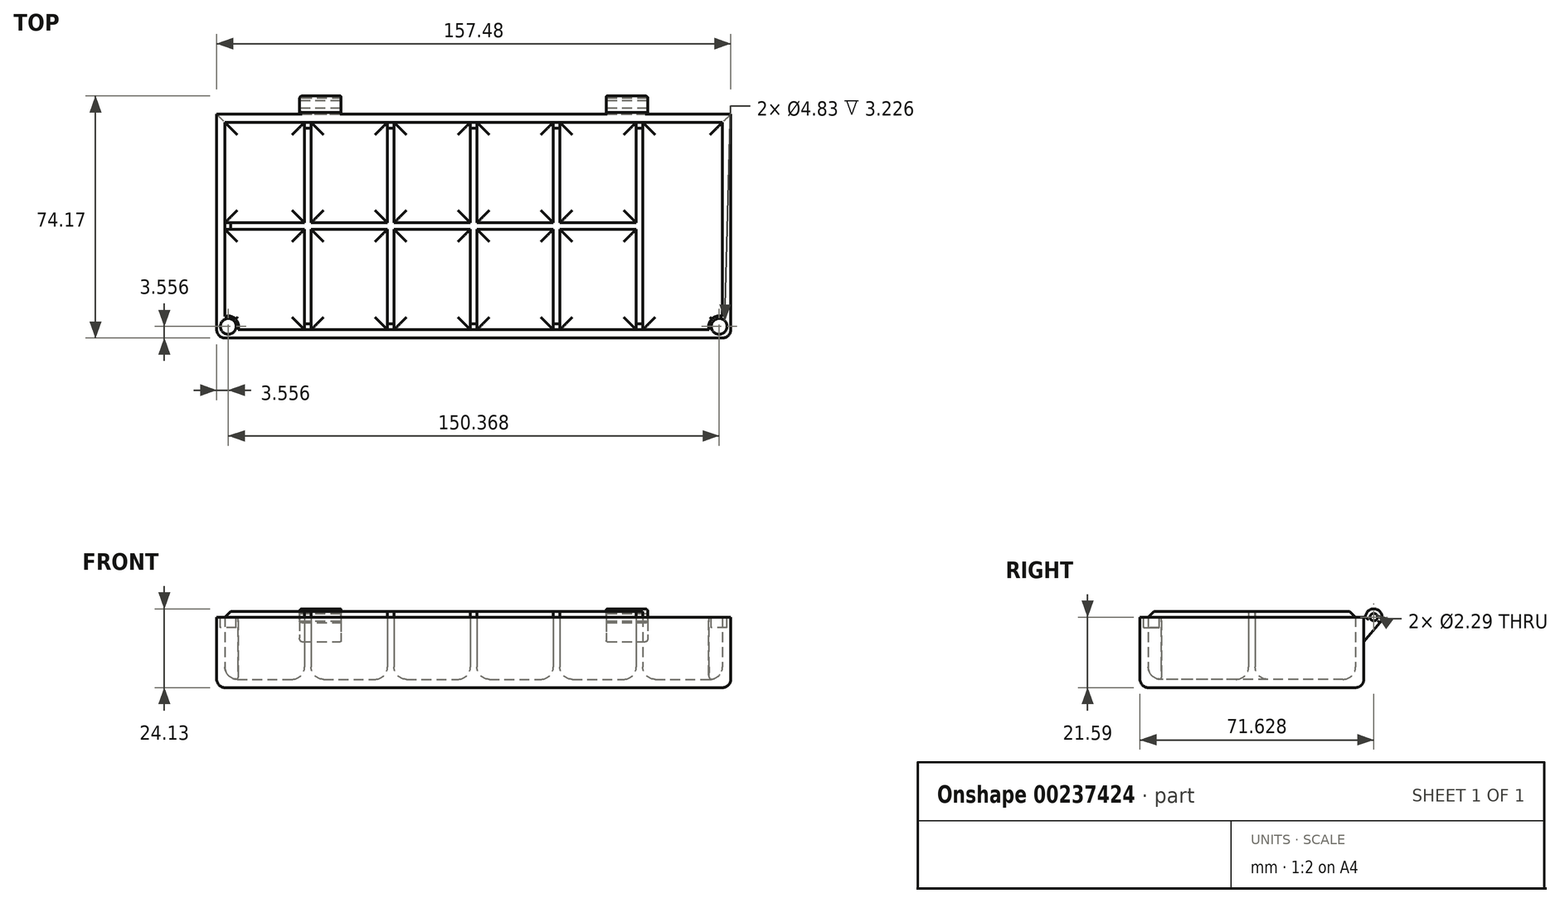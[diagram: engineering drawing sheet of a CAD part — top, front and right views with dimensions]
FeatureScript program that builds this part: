
annotation { "Feature Type Name" : "Feature", "Feature Type Description" : "" }
export const myFeature = defineFeature(function(context is Context, id is Id, definition is map)
    precondition{}
    {
        {
            var Q0;
            Q0=qCreatedBy(makeId("Top.planeOp"),FACE);
            var sketch = newSketch(context, id + "F0", { "sketchPlane" : qUnion([Q0])});
            skLineSegment(sketch, "E0.bottom", {"start": v(-78.74, 34.29) * mm, "end": v(78.74, 34.3) * mm});
            skLineSegment(sketch, "E0.top", {"start": v(-78.74, -34.3) * mm, "end": v(78.74, -34.3) * mm});
            skLineSegment(sketch, "E0.left", {"start": v(-78.74, 34.29) * mm, "end": v(-78.74, -34.3) * mm});
            skLineSegment(sketch, "E0.right", {"start": v(78.74, 34.3) * mm, "end": v(78.74, -34.3) * mm});
            skSolve(sketch);
        }
        {
            var Q0;
            Q0 = qSketchRegion(id + "F0", true);
            extrude(context, id + "F1", {"entities" : qUnion([Q0]), "depth" : 2.54 * mm});
        }
        {
            var Q0;
            Q0=makeQuery(id+"F1.opExtrude","CAP_FACE",FACE,{"disambiguationData":[OSD([sQuery(id+"F0.wireOp",EDGE,"E0.bottom"),sQuery(id+"F0.wireOp",EDGE,"E0.top"),sQuery(id+"F0.wireOp",EDGE,"E0.left"),sQuery(id+"F0.wireOp",EDGE,"E0.right")])],"isStart":false});
            var sketch = newSketch(context, id + "F2", { "sketchPlane" : qUnion([Q0])});
            skLineSegment(sketch, "E1.bottom", {"start": v(-78.74, 34.29) * mm, "end": v(78.74, 34.29) * mm});
            skLineSegment(sketch, "E1.top", {"start": v(-78.74, -34.3) * mm, "end": v(78.74, -34.3) * mm});
            skLineSegment(sketch, "E1.left", {"start": v(-78.74, 34.29) * mm, "end": v(-78.74, -34.3) * mm});
            skLineSegment(sketch, "E1.right", {"start": v(78.74, 34.29) * mm, "end": v(78.74, -34.3) * mm});
            skLineSegment(sketch, "E2.bottom", {"start": v(-76.2, 31.75) * mm, "end": v(-51.82, 31.75) * mm});
            skLineSegment(sketch, "E2.top", {"start": v(-76.2, -31.75) * mm, "end": v(-51.82, -31.75) * mm});
            skLineSegment(sketch, "E2.left", {"start": v(-76.2, 31.75) * mm, "end": v(-76.2, 1.02) * mm});
            skLineSegment(sketch, "E2.right", {"start": v(76.2, 31.75) * mm, "end": v(76.2, -31.75) * mm});
            skLineSegment(sketch, "E3", {"start": v(-76.2, 1.02) * mm, "end": v(-51.82, 1.02) * mm});
            skLineSegment(sketch, "E4", {"start": v(-76.2, -1.02) * mm, "end": v(-51.82, -1.02) * mm});
            skLineSegment(sketch, "E5", {"start": v(-51.82, 31.75) * mm, "end": v(-51.82, 1.02) * mm});
            skLineSegment(sketch, "E6", {"start": v(-49.78, 31.75) * mm, "end": v(-49.78, 1.02) * mm});
            skLineSegment(sketch, "E7.trimOffspring", {"start": v(-51.82, -1.02) * mm, "end": v(-51.82, -31.75) * mm});
            skLineSegment(sketch, "E8.trimOffspring", {"start": v(-49.78, -1.02) * mm, "end": v(-49.78, -31.75) * mm});
            skLineSegment(sketch, "E9.trimOffspring", {"start": v(-49.78, 1.02) * mm, "end": v(-26.42, 1.02) * mm});
            skLineSegment(sketch, "E10.trimOffspring", {"start": v(-49.78, -1.02) * mm, "end": v(-26.42, -1.02) * mm});
            skLineSegment(sketch, "E11.trimOffspring", {"start": v(-76.2, -1.02) * mm, "end": v(-76.2, -31.75) * mm});
            skLineSegment(sketch, "E12.trimOffspring", {"start": v(-49.78, -31.75) * mm, "end": v(-26.42, -31.75) * mm});
            skLineSegment(sketch, "E13.trimOffspring", {"start": v(-49.78, 31.75) * mm, "end": v(-26.42, 31.75) * mm});
            skLineSegment(sketch, "E14.1.0.0", {"start": v(-24.38, 31.75) * mm, "end": v(-24.38, 1.02) * mm});
            skLineSegment(sketch, "E14.1.0.1", {"start": v(-26.42, 31.75) * mm, "end": v(-26.42, 1.02) * mm});
            skLineSegment(sketch, "E14.1.0.2", {"start": v(-24.38, -1.02) * mm, "end": v(-24.38, -31.75) * mm});
            skLineSegment(sketch, "E14.1.0.3", {"start": v(-26.42, -1.02) * mm, "end": v(-26.42, -31.75) * mm});
            skLineSegment(sketch, "E14.2.0.0", {"start": v(1.02, 31.75) * mm, "end": v(1.02, 1.02) * mm});
            skLineSegment(sketch, "E14.2.0.1", {"start": v(-1.02, 31.75) * mm, "end": v(-1.02, 1.02) * mm});
            skLineSegment(sketch, "E14.2.0.2", {"start": v(1.02, -1.02) * mm, "end": v(1.02, -31.75) * mm});
            skLineSegment(sketch, "E14.2.0.3", {"start": v(-1.02, -1.02) * mm, "end": v(-1.02, -31.75) * mm});
            skLineSegment(sketch, "E14.3.0.0", {"start": v(26.42, 31.75) * mm, "end": v(26.42, 1.02) * mm});
            skLineSegment(sketch, "E14.3.0.1", {"start": v(24.38, 31.75) * mm, "end": v(24.38, 1.02) * mm});
            skLineSegment(sketch, "E14.3.0.2", {"start": v(26.42, -1.02) * mm, "end": v(26.42, -31.75) * mm});
            skLineSegment(sketch, "E14.3.0.3", {"start": v(24.38, -1.02) * mm, "end": v(24.38, -31.75) * mm});
            skLineSegment(sketch, "E14.4.0.0", {"start": v(51.82, 31.75) * mm, "end": v(51.82, 1.02) * mm});
            skLineSegment(sketch, "E14.4.0.1", {"start": v(49.78, 31.75) * mm, "end": v(49.78, 1.02) * mm});
            skLineSegment(sketch, "E14.4.0.2", {"start": v(51.82, -1.02) * mm, "end": v(51.82, -31.75) * mm});
            skLineSegment(sketch, "E14.4.0.3", {"start": v(49.78, -1.02) * mm, "end": v(49.78, -31.75) * mm});
            skLineSegment(sketch, "E14.direction1", {"start": v(-51.82, -31.75) * mm, "end": v(-26.42, -31.75) * mm, "construction": true});
            skLineSegment(sketch, "E15.trimOffspring", {"start": v(-24.38, -31.75) * mm, "end": v(-1.02, -31.75) * mm});
            skLineSegment(sketch, "E16.trimOffspring", {"start": v(1.02, -31.75) * mm, "end": v(24.38, -31.75) * mm});
            skLineSegment(sketch, "E17.trimOffspring", {"start": v(26.42, -31.75) * mm, "end": v(49.78, -31.75) * mm});
            skLineSegment(sketch, "E18.trimOffspring", {"start": v(51.82, -31.75) * mm, "end": v(76.2, -31.75) * mm});
            skLineSegment(sketch, "E19.trimOffspring", {"start": v(26.42, 1.02) * mm, "end": v(49.78, 1.02) * mm});
            skLineSegment(sketch, "E20.trimOffspring", {"start": v(26.42, -1.02) * mm, "end": v(49.78, -1.02) * mm});
            skLineSegment(sketch, "E21.trimOffspring", {"start": v(1.02, 1.02) * mm, "end": v(24.38, 1.02) * mm});
            skLineSegment(sketch, "E22.trimOffspring", {"start": v(1.02, -1.02) * mm, "end": v(24.38, -1.02) * mm});
            skLineSegment(sketch, "E23.trimOffspring", {"start": v(-24.38, 1.02) * mm, "end": v(-1.02, 1.02) * mm});
            skLineSegment(sketch, "E24.trimOffspring", {"start": v(-24.38, -1.02) * mm, "end": v(-1.02, -1.02) * mm});
            skLineSegment(sketch, "E25.trimOffspring", {"start": v(-24.38, 31.75) * mm, "end": v(-1.02, 31.75) * mm});
            skLineSegment(sketch, "E26.trimOffspring", {"start": v(1.02, 31.75) * mm, "end": v(24.38, 31.75) * mm});
            skLineSegment(sketch, "E27.trimOffspring", {"start": v(26.42, 31.75) * mm, "end": v(49.78, 31.75) * mm});
            skLineSegment(sketch, "E28.trimOffspring", {"start": v(51.82, 31.75) * mm, "end": v(76.2, 31.75) * mm});
            skLineSegment(sketch, "E29", {"start": v(51.82, 1.02) * mm, "end": v(51.82, -1.02) * mm});
            skSolve(sketch);
        }
        {
            var Q0;
            Q0 = qSketchRegion(id + "F2", true);
            extrude(context, id + "F3", {"entities" : qUnion([Q0]), "operationType" : NewBodyOperationType.ADD, "depth" : 19.05 * mm});
        }
        {
            var Q0;
            Q0=makeQuery(id+"F3.boolean.opBoolean","SPLIT",FACE,{"disambiguationData":[TD([makeQuery(id+"F3.opExtrude","SWEPT_FACE",FACE,{"disambiguationData":[OSD([sQuery(id+"F2.wireOp",EDGE,"E2.bottom")])]})])],"derivedFrom":makeQuery(id+"F1.opExtrude","CAP_FACE",FACE,{"disambiguationData":[OSD([sQuery(id+"F0.wireOp",EDGE,"E0.bottom"),sQuery(id+"F0.wireOp",EDGE,"E0.top"),sQuery(id+"F0.wireOp",EDGE,"E0.left"),sQuery(id+"F0.wireOp",EDGE,"E0.right")])],"isStart":false})});
            var Q1;
            Q1=makeQuery(id+"F3.boolean.opBoolean","SPLIT",FACE,{"disambiguationData":[TD([makeQuery(id+"F3.opExtrude","SWEPT_FACE",FACE,{"disambiguationData":[OSD([sQuery(id+"F2.wireOp",EDGE,"E2.top")])]})])],"derivedFrom":makeQuery(id+"F1.opExtrude","CAP_FACE",FACE,{"disambiguationData":[OSD([sQuery(id+"F0.wireOp",EDGE,"E0.bottom"),sQuery(id+"F0.wireOp",EDGE,"E0.top"),sQuery(id+"F0.wireOp",EDGE,"E0.left"),sQuery(id+"F0.wireOp",EDGE,"E0.right")])],"isStart":false})});
            var Q2;
            Q2=makeQuery(id+"F3.boolean.opBoolean","SPLIT",FACE,{"disambiguationData":[TD([makeQuery(id+"F3.opExtrude","SWEPT_FACE",FACE,{"disambiguationData":[OSD([sQuery(id+"F2.wireOp",EDGE,"E8.trimOffspring")])]})])],"derivedFrom":makeQuery(id+"F1.opExtrude","CAP_FACE",FACE,{"disambiguationData":[OSD([sQuery(id+"F0.wireOp",EDGE,"E0.bottom"),sQuery(id+"F0.wireOp",EDGE,"E0.top"),sQuery(id+"F0.wireOp",EDGE,"E0.left"),sQuery(id+"F0.wireOp",EDGE,"E0.right")])],"isStart":false})});
            var Q3;
            Q3=makeQuery(id+"F3.boolean.opBoolean","SPLIT",FACE,{"disambiguationData":[TD([makeQuery(id+"F3.opExtrude","SWEPT_FACE",FACE,{"disambiguationData":[OSD([sQuery(id+"F2.wireOp",EDGE,"E6")])]})])],"derivedFrom":makeQuery(id+"F1.opExtrude","CAP_FACE",FACE,{"disambiguationData":[OSD([sQuery(id+"F0.wireOp",EDGE,"E0.bottom"),sQuery(id+"F0.wireOp",EDGE,"E0.top"),sQuery(id+"F0.wireOp",EDGE,"E0.left"),sQuery(id+"F0.wireOp",EDGE,"E0.right")])],"isStart":false})});
            var Q4;
            Q4=makeQuery(id+"F3.boolean.opBoolean","SPLIT",FACE,{"disambiguationData":[TD([makeQuery(id+"F3.opExtrude","SWEPT_FACE",FACE,{"disambiguationData":[OSD([sQuery(id+"F2.wireOp",EDGE,"E14.1.0.0")])]})])],"derivedFrom":makeQuery(id+"F1.opExtrude","CAP_FACE",FACE,{"disambiguationData":[OSD([sQuery(id+"F0.wireOp",EDGE,"E0.bottom"),sQuery(id+"F0.wireOp",EDGE,"E0.top"),sQuery(id+"F0.wireOp",EDGE,"E0.left"),sQuery(id+"F0.wireOp",EDGE,"E0.right")])],"isStart":false})});
            var Q5;
            Q5=makeQuery(id+"F3.boolean.opBoolean","SPLIT",FACE,{"disambiguationData":[TD([makeQuery(id+"F3.opExtrude","SWEPT_FACE",FACE,{"disambiguationData":[OSD([sQuery(id+"F2.wireOp",EDGE,"E14.1.0.2")])]})])],"derivedFrom":makeQuery(id+"F1.opExtrude","CAP_FACE",FACE,{"disambiguationData":[OSD([sQuery(id+"F0.wireOp",EDGE,"E0.bottom"),sQuery(id+"F0.wireOp",EDGE,"E0.top"),sQuery(id+"F0.wireOp",EDGE,"E0.left"),sQuery(id+"F0.wireOp",EDGE,"E0.right")])],"isStart":false})});
            var Q6;
            Q6=makeQuery(id+"F3.boolean.opBoolean","SPLIT",FACE,{"disambiguationData":[TD([makeQuery(id+"F3.opExtrude","SWEPT_FACE",FACE,{"disambiguationData":[OSD([sQuery(id+"F2.wireOp",EDGE,"E14.2.0.2")])]})])],"derivedFrom":makeQuery(id+"F1.opExtrude","CAP_FACE",FACE,{"disambiguationData":[OSD([sQuery(id+"F0.wireOp",EDGE,"E0.bottom"),sQuery(id+"F0.wireOp",EDGE,"E0.top"),sQuery(id+"F0.wireOp",EDGE,"E0.left"),sQuery(id+"F0.wireOp",EDGE,"E0.right")])],"isStart":false})});
            var Q7;
            Q7=makeQuery(id+"F3.boolean.opBoolean","SPLIT",FACE,{"disambiguationData":[TD([makeQuery(id+"F3.opExtrude","SWEPT_FACE",FACE,{"disambiguationData":[OSD([sQuery(id+"F2.wireOp",EDGE,"E14.2.0.0")])]})])],"derivedFrom":makeQuery(id+"F1.opExtrude","CAP_FACE",FACE,{"disambiguationData":[OSD([sQuery(id+"F0.wireOp",EDGE,"E0.bottom"),sQuery(id+"F0.wireOp",EDGE,"E0.top"),sQuery(id+"F0.wireOp",EDGE,"E0.left"),sQuery(id+"F0.wireOp",EDGE,"E0.right")])],"isStart":false})});
            var Q8;
            Q8=makeQuery(id+"F3.boolean.opBoolean","SPLIT",FACE,{"disambiguationData":[TD([makeQuery(id+"F3.opExtrude","SWEPT_FACE",FACE,{"disambiguationData":[OSD([sQuery(id+"F2.wireOp",EDGE,"E14.3.0.0")])]})])],"derivedFrom":makeQuery(id+"F1.opExtrude","CAP_FACE",FACE,{"disambiguationData":[OSD([sQuery(id+"F0.wireOp",EDGE,"E0.bottom"),sQuery(id+"F0.wireOp",EDGE,"E0.top"),sQuery(id+"F0.wireOp",EDGE,"E0.left"),sQuery(id+"F0.wireOp",EDGE,"E0.right")])],"isStart":false})});
            var Q9;
            Q9=makeQuery(id+"F3.boolean.opBoolean","SPLIT",FACE,{"disambiguationData":[TD([makeQuery(id+"F3.opExtrude","SWEPT_FACE",FACE,{"disambiguationData":[OSD([sQuery(id+"F2.wireOp",EDGE,"E14.3.0.2")])]})])],"derivedFrom":makeQuery(id+"F1.opExtrude","CAP_FACE",FACE,{"disambiguationData":[OSD([sQuery(id+"F0.wireOp",EDGE,"E0.bottom"),sQuery(id+"F0.wireOp",EDGE,"E0.top"),sQuery(id+"F0.wireOp",EDGE,"E0.left"),sQuery(id+"F0.wireOp",EDGE,"E0.right")])],"isStart":false})});
            var Q10;
            Q10=makeQuery(id+"F3.boolean.opBoolean","SPLIT",FACE,{"disambiguationData":[TD([makeQuery(id+"F3.opExtrude","SWEPT_FACE",FACE,{"disambiguationData":[OSD([sQuery(id+"F2.wireOp",EDGE,"E2.right")])]})])],"derivedFrom":makeQuery(id+"F1.opExtrude","CAP_FACE",FACE,{"disambiguationData":[OSD([sQuery(id+"F0.wireOp",EDGE,"E0.bottom"),sQuery(id+"F0.wireOp",EDGE,"E0.top"),sQuery(id+"F0.wireOp",EDGE,"E0.left"),sQuery(id+"F0.wireOp",EDGE,"E0.right")])],"isStart":false})});
            fillet(context, id + "F4", {"entities" : qUnion([Q0, Q1, Q2, Q3, Q4, Q5, Q6, Q7, Q8, Q9, Q10]), "radius" : 3.8 * mm, "tangentPropagation" : true, "allowEdgeOverflow" : false});
        }
        {
            var Q0;
            Q0=makeQuery(id+"F3.boolean.opBoolean","MERGE",FACE,{"derivedFrom":[makeQuery(id+"F1.opExtrude","SWEPT_FACE",FACE,{"disambiguationData":[OSD([sQuery(id+"F0.wireOp",EDGE,"E0.right")])]}),makeQuery(id+"F3.opExtrude","SWEPT_FACE",FACE,{"disambiguationData":[OSD([sQuery(id+"F2.wireOp",EDGE,"E1.right")])]})]});
            var sketch = newSketch(context, id + "F5", { "sketchPlane" : qUnion([Q0])});
            skCircle(sketch, "E30", {"center": v(37.34, 21.59) * mm, "radius": 1.14 * mm});
            skLineSegment(sketch, "E31", {"start": v(38.57, 24.13) * mm, "end": v(38.57, 24.13) * mm});
            skLineSegment(sketch, "E32", {"start": v(39.24, 19.9) * mm, "end": v(34.3, 14) * mm});
            skArc(sketch, "E33", {"start": v(39.24, 19.9) * mm, "mid": v(38.24, 23.96) * mm, "end": v(34.8, 21.59) * mm});
            skLineSegment(sketch, "E34", {"start": v(34.8, 21.59) * mm, "end": v(34.3, 21.59) * mm});
            skLineSegment(sketch, "E35", {"start": v(34.3, 21.59) * mm, "end": v(34.3, 14) * mm});
            skSolve(sketch);
        }
        {
            var Q0;
            Q0 = qSketchRegion(id + "F5", true);
            var Q1;
            Q1=makeQuery(id+"F3.boolean.opBoolean","MERGE",FACE,{"derivedFrom":[makeQuery(id+"F1.opExtrude","SWEPT_FACE",FACE,{"disambiguationData":[OSD([sQuery(id+"F0.wireOp",EDGE,"E0.left")])]}),makeQuery(id+"F3.opExtrude","SWEPT_FACE",FACE,{"disambiguationData":[OSD([sQuery(id+"F2.wireOp",EDGE,"E1.left")])]})]});
            extrude(context, id + "F6", {"entities" : qUnion([Q0]), "operationType" : NewBodyOperationType.ADD, "endBound" : BoundingType.UP_TO_SURFACE, "oppositeDirection" : true, "endBoundEntityFace" : qUnion([Q1]), "depth" : 25.4 * mm});
        }
        {
            var Q0;
            Q0=makeQuery(id+"F1.opExtrude","CAP_FACE",FACE,{"disambiguationData":[OSD([sQuery(id+"F0.wireOp",EDGE,"E0.bottom"),sQuery(id+"F0.wireOp",EDGE,"E0.top"),sQuery(id+"F0.wireOp",EDGE,"E0.left"),sQuery(id+"F0.wireOp",EDGE,"E0.right")])],"isStart":true});
            var sketch = newSketch(context, id + "F7", { "sketchPlane" : qUnion([Q0])});
            skLineSegment(sketch, "E36.bottom", {"start": v(-78.74, -34.29) * mm, "end": v(-53.34, -34.29) * mm});
            skLineSegment(sketch, "E36.top", {"start": v(-78.74, -46.99) * mm, "end": v(-53.34, -46.99) * mm});
            skLineSegment(sketch, "E36.left", {"start": v(-78.74, -34.29) * mm, "end": v(-78.74, -46.99) * mm});
            skLineSegment(sketch, "E36.right", {"start": v(-53.34, -34.29) * mm, "end": v(-53.34, -46.99) * mm});
            skLineSegment(sketch, "E37.bottom", {"start": v(78.74, -34.3) * mm, "end": v(53.34, -34.3) * mm});
            skLineSegment(sketch, "E37.top", {"start": v(78.74, -47) * mm, "end": v(53.34, -47) * mm});
            skLineSegment(sketch, "E37.left", {"start": v(78.74, -34.3) * mm, "end": v(78.74, -47) * mm});
            skLineSegment(sketch, "E37.right", {"start": v(53.34, -34.3) * mm, "end": v(53.34, -47) * mm});
            skLineSegment(sketch, "E38.bottom", {"start": v(-40.64, -34.3) * mm, "end": v(40.64, -34.3) * mm});
            skLineSegment(sketch, "E38.top", {"start": v(-40.64, -47) * mm, "end": v(40.64, -47) * mm});
            skLineSegment(sketch, "E38.left", {"start": v(-40.64, -34.3) * mm, "end": v(-40.64, -47) * mm});
            skLineSegment(sketch, "E38.right", {"start": v(40.64, -34.3) * mm, "end": v(40.64, -47) * mm});
            skSolve(sketch);
        }
        {
            var Q0;
            Q0 = qSketchRegion(id + "F7", true);
            extrude(context, id + "F8", {"entities" : qUnion([Q0]), "operationType" : NewBodyOperationType.REMOVE, "oppositeDirection" : true, "depth" : 38.1 * mm});
        }
        {
            var Q0;
            {var subQ0=sQuery(id+"F0.wireOp",EDGE,"E0.right");Q0=makeQuery(id+"F8.boolean.opBoolean","MERGE",EDGE,{"derivedFrom":[makeQuery(id+"F3.boolean.opBoolean","MERGE",EDGE,{"derivedFrom":[makeQuery(id+"F1.opExtrude","SWEPT_EDGE",EDGE,{"disambiguationData":[OSD([sQuery(id+"F0.wireOp",EDGE,"E0.bottom"),subQ0])]}),makeQuery(id+"F3.opExtrude","SWEPT_EDGE",EDGE,{"disambiguationData":[OSD([sQuery(id+"F2.wireOp",EDGE,"E1.bottom"),sQuery(id+"F2.wireOp",EDGE,"E1.right")])]})]}),makeQuery(id+"F8.opExtrude","SWEPT_EDGE",EDGE,{"disambiguationData":[OSD([subQ0,sQuery(id+"F7.wireOp",EDGE,"E37.bottom"),sQuery(id+"F7.wireOp",EDGE,"E37.left")])]})]});}
            var Q1;
            Q1=makeQuery(id+"F3.boolean.opBoolean","MERGE",EDGE,{"derivedFrom":[makeQuery(id+"F1.opExtrude","SWEPT_EDGE",EDGE,{"disambiguationData":[OSD([sQuery(id+"F0.wireOp",EDGE,"E0.top"),sQuery(id+"F0.wireOp",EDGE,"E0.right")])]}),makeQuery(id+"F3.opExtrude","SWEPT_EDGE",EDGE,{"disambiguationData":[OSD([sQuery(id+"F2.wireOp",EDGE,"E1.top"),sQuery(id+"F2.wireOp",EDGE,"E1.right")])]})]});
            var Q2;
            Q2=makeQuery(id+"F3.boolean.opBoolean","MERGE",EDGE,{"derivedFrom":[makeQuery(id+"F1.opExtrude","SWEPT_EDGE",EDGE,{"disambiguationData":[OSD([sQuery(id+"F0.wireOp",EDGE,"E0.top"),sQuery(id+"F0.wireOp",EDGE,"E0.left")])]}),makeQuery(id+"F3.opExtrude","SWEPT_EDGE",EDGE,{"disambiguationData":[OSD([sQuery(id+"F2.wireOp",EDGE,"E1.top"),sQuery(id+"F2.wireOp",EDGE,"E1.left")])]})]});
            var Q3;
            {var subQ0=sQuery(id+"F0.wireOp",EDGE,"E0.left");Q3=makeQuery(id+"F8.boolean.opBoolean","MERGE",EDGE,{"derivedFrom":[makeQuery(id+"F3.boolean.opBoolean","MERGE",EDGE,{"derivedFrom":[makeQuery(id+"F1.opExtrude","SWEPT_EDGE",EDGE,{"disambiguationData":[OSD([sQuery(id+"F0.wireOp",EDGE,"E0.bottom"),subQ0])]}),makeQuery(id+"F3.opExtrude","SWEPT_EDGE",EDGE,{"disambiguationData":[OSD([sQuery(id+"F2.wireOp",EDGE,"E1.bottom"),sQuery(id+"F2.wireOp",EDGE,"E1.left")])]})]}),makeQuery(id+"F8.opExtrude","SWEPT_EDGE",EDGE,{"disambiguationData":[OSD([subQ0,sQuery(id+"F7.wireOp",EDGE,"E36.bottom"),sQuery(id+"F7.wireOp",EDGE,"E36.left")])]})]});}
            var Q4;
            Q4=makeQuery(id+"F1.opExtrude","CAP_FACE",FACE,{"disambiguationData":[OSD([sQuery(id+"F0.wireOp",EDGE,"E0.bottom"),sQuery(id+"F0.wireOp",EDGE,"E0.top"),sQuery(id+"F0.wireOp",EDGE,"E0.left"),sQuery(id+"F0.wireOp",EDGE,"E0.right")])],"isStart":true});
            fillet(context, id + "F9", {"entities" : qUnion([Q0, Q1, Q2, Q3, Q4]), "radius" : 2.54 * mm, "tangentPropagation" : true, "allowEdgeOverflow" : false});
        }
        {
            var Q0;
            Q0=makeQuery(id+"F8.boolean.opBoolean","INTERSECT",EDGE,{"derivedFrom":[makeQuery(id+"F6.opExtrude","SWEPT_FACE",FACE,{"disambiguationData":[OSD([sQuery(id+"F5.wireOp",EDGE,"E32")])]}),makeQuery(id+"F8.opExtrude","SWEPT_FACE",FACE,{"disambiguationData":[OSD([sQuery(id+"F7.wireOp",EDGE,"E38.left")])]})]});
            var Q1;
            Q1=makeQuery(id+"F8.boolean.opBoolean","INTERSECT",EDGE,{"derivedFrom":[makeQuery(id+"F6.opExtrude","SWEPT_FACE",FACE,{"disambiguationData":[OSD([sQuery(id+"F5.wireOp",EDGE,"E33")])]}),makeQuery(id+"F8.opExtrude","SWEPT_FACE",FACE,{"disambiguationData":[OSD([sQuery(id+"F7.wireOp",EDGE,"E38.left")])]})]});
            var Q2;
            Q2=makeQuery(id+"F8.boolean.opBoolean","INTERSECT",EDGE,{"derivedFrom":[makeQuery(id+"F6.opExtrude","SWEPT_FACE",FACE,{"disambiguationData":[OSD([sQuery(id+"F5.wireOp",EDGE,"E30")])]}),makeQuery(id+"F8.opExtrude","SWEPT_FACE",FACE,{"disambiguationData":[OSD([sQuery(id+"F7.wireOp",EDGE,"E38.left")])]})]});
            var Q3;
            Q3=makeQuery(id+"F8.boolean.opBoolean","INTERSECT",EDGE,{"derivedFrom":[makeQuery(id+"F6.opExtrude","SWEPT_FACE",FACE,{"disambiguationData":[OSD([sQuery(id+"F5.wireOp",EDGE,"E30")])]}),makeQuery(id+"F8.opExtrude","SWEPT_FACE",FACE,{"disambiguationData":[OSD([sQuery(id+"F7.wireOp",EDGE,"E38.right")])]})]});
            var Q4;
            Q4=makeQuery(id+"F8.boolean.opBoolean","INTERSECT",EDGE,{"derivedFrom":[makeQuery(id+"F6.opExtrude","SWEPT_FACE",FACE,{"disambiguationData":[OSD([sQuery(id+"F5.wireOp",EDGE,"E33")])]}),makeQuery(id+"F8.opExtrude","SWEPT_FACE",FACE,{"disambiguationData":[OSD([sQuery(id+"F7.wireOp",EDGE,"E38.right")])]})]});
            var Q5;
            Q5=makeQuery(id+"F8.boolean.opBoolean","INTERSECT",EDGE,{"derivedFrom":[makeQuery(id+"F6.boolean.opBoolean","MERGE",FACE,{"derivedFrom":[makeQuery(id+"F3.opExtrude","CAP_FACE",FACE,{"disambiguationData":[OSD([sQuery(id+"F2.wireOp",EDGE,"E1.bottom"),sQuery(id+"F2.wireOp",EDGE,"E1.top"),sQuery(id+"F2.wireOp",EDGE,"E1.left"),sQuery(id+"F2.wireOp",EDGE,"E1.right"),sQuery(id+"F2.wireOp",EDGE,"E2.bottom"),sQuery(id+"F2.wireOp",EDGE,"E2.top"),sQuery(id+"F2.wireOp",EDGE,"E2.left"),sQuery(id+"F2.wireOp",EDGE,"E2.right"),sQuery(id+"F2.wireOp",EDGE,"E3"),sQuery(id+"F2.wireOp",EDGE,"E4"),sQuery(id+"F2.wireOp",EDGE,"E5"),sQuery(id+"F2.wireOp",EDGE,"E6"),sQuery(id+"F2.wireOp",EDGE,"E7.trimOffspring"),sQuery(id+"F2.wireOp",EDGE,"E8.trimOffspring"),sQuery(id+"F2.wireOp",EDGE,"E9.trimOffspring"),sQuery(id+"F2.wireOp",EDGE,"E10.trimOffspring"),sQuery(id+"F2.wireOp",EDGE,"E11.trimOffspring"),sQuery(id+"F2.wireOp",EDGE,"E12.trimOffspring"),sQuery(id+"F2.wireOp",EDGE,"E13.trimOffspring"),sQuery(id+"F2.wireOp",EDGE,"E14.1.0.0"),sQuery(id+"F2.wireOp",EDGE,"E14.1.0.1"),sQuery(id+"F2.wireOp",EDGE,"E14.1.0.2"),sQuery(id+"F2.wireOp",EDGE,"E14.1.0.3"),sQuery(id+"F2.wireOp",EDGE,"E14.2.0.0"),sQuery(id+"F2.wireOp",EDGE,"E14.2.0.1"),sQuery(id+"F2.wireOp",EDGE,"E14.2.0.2"),sQuery(id+"F2.wireOp",EDGE,"E14.2.0.3"),sQuery(id+"F2.wireOp",EDGE,"E14.3.0.0"),sQuery(id+"F2.wireOp",EDGE,"E14.3.0.1"),sQuery(id+"F2.wireOp",EDGE,"E14.3.0.2"),sQuery(id+"F2.wireOp",EDGE,"E14.3.0.3"),sQuery(id+"F2.wireOp",EDGE,"E14.4.0.0"),sQuery(id+"F2.wireOp",EDGE,"E14.4.0.1"),sQuery(id+"F2.wireOp",EDGE,"E14.4.0.2"),sQuery(id+"F2.wireOp",EDGE,"E14.4.0.3"),sQuery(id+"F2.wireOp",EDGE,"E15.trimOffspring"),sQuery(id+"F2.wireOp",EDGE,"E16.trimOffspring"),sQuery(id+"F2.wireOp",EDGE,"E17.trimOffspring"),sQuery(id+"F2.wireOp",EDGE,"E18.trimOffspring"),sQuery(id+"F2.wireOp",EDGE,"E19.trimOffspring"),sQuery(id+"F2.wireOp",EDGE,"E20.trimOffspring"),sQuery(id+"F2.wireOp",EDGE,"E21.trimOffspring"),sQuery(id+"F2.wireOp",EDGE,"E22.trimOffspring"),sQuery(id+"F2.wireOp",EDGE,"E23.trimOffspring"),sQuery(id+"F2.wireOp",EDGE,"E24.trimOffspring"),sQuery(id+"F2.wireOp",EDGE,"E25.trimOffspring"),sQuery(id+"F2.wireOp",EDGE,"E26.trimOffspring"),sQuery(id+"F2.wireOp",EDGE,"E27.trimOffspring"),sQuery(id+"F2.wireOp",EDGE,"E28.trimOffspring"),sQuery(id+"F2.wireOp",EDGE,"E29")])],"isStart":false}),makeQuery(id+"F6.opExtrude","SWEPT_FACE",FACE,{"disambiguationData":[OSD([sQuery(id+"F5.wireOp",EDGE,"E34")])]})]}),makeQuery(id+"F8.opExtrude","SWEPT_FACE",FACE,{"disambiguationData":[OSD([sQuery(id+"F7.wireOp",EDGE,"E38.right")])]})]});
            var Q6;
            Q6=makeQuery(id+"F8.boolean.opBoolean","INTERSECT",EDGE,{"derivedFrom":[makeQuery(id+"F6.boolean.opBoolean","MERGE",FACE,{"derivedFrom":[makeQuery(id+"F3.opExtrude","CAP_FACE",FACE,{"disambiguationData":[OSD([sQuery(id+"F2.wireOp",EDGE,"E1.bottom"),sQuery(id+"F2.wireOp",EDGE,"E1.top"),sQuery(id+"F2.wireOp",EDGE,"E1.left"),sQuery(id+"F2.wireOp",EDGE,"E1.right"),sQuery(id+"F2.wireOp",EDGE,"E2.bottom"),sQuery(id+"F2.wireOp",EDGE,"E2.top"),sQuery(id+"F2.wireOp",EDGE,"E2.left"),sQuery(id+"F2.wireOp",EDGE,"E2.right"),sQuery(id+"F2.wireOp",EDGE,"E3"),sQuery(id+"F2.wireOp",EDGE,"E4"),sQuery(id+"F2.wireOp",EDGE,"E5"),sQuery(id+"F2.wireOp",EDGE,"E6"),sQuery(id+"F2.wireOp",EDGE,"E7.trimOffspring"),sQuery(id+"F2.wireOp",EDGE,"E8.trimOffspring"),sQuery(id+"F2.wireOp",EDGE,"E9.trimOffspring"),sQuery(id+"F2.wireOp",EDGE,"E10.trimOffspring"),sQuery(id+"F2.wireOp",EDGE,"E11.trimOffspring"),sQuery(id+"F2.wireOp",EDGE,"E12.trimOffspring"),sQuery(id+"F2.wireOp",EDGE,"E13.trimOffspring"),sQuery(id+"F2.wireOp",EDGE,"E14.1.0.0"),sQuery(id+"F2.wireOp",EDGE,"E14.1.0.1"),sQuery(id+"F2.wireOp",EDGE,"E14.1.0.2"),sQuery(id+"F2.wireOp",EDGE,"E14.1.0.3"),sQuery(id+"F2.wireOp",EDGE,"E14.2.0.0"),sQuery(id+"F2.wireOp",EDGE,"E14.2.0.1"),sQuery(id+"F2.wireOp",EDGE,"E14.2.0.2"),sQuery(id+"F2.wireOp",EDGE,"E14.2.0.3"),sQuery(id+"F2.wireOp",EDGE,"E14.3.0.0"),sQuery(id+"F2.wireOp",EDGE,"E14.3.0.1"),sQuery(id+"F2.wireOp",EDGE,"E14.3.0.2"),sQuery(id+"F2.wireOp",EDGE,"E14.3.0.3"),sQuery(id+"F2.wireOp",EDGE,"E14.4.0.0"),sQuery(id+"F2.wireOp",EDGE,"E14.4.0.1"),sQuery(id+"F2.wireOp",EDGE,"E14.4.0.2"),sQuery(id+"F2.wireOp",EDGE,"E14.4.0.3"),sQuery(id+"F2.wireOp",EDGE,"E15.trimOffspring"),sQuery(id+"F2.wireOp",EDGE,"E16.trimOffspring"),sQuery(id+"F2.wireOp",EDGE,"E17.trimOffspring"),sQuery(id+"F2.wireOp",EDGE,"E18.trimOffspring"),sQuery(id+"F2.wireOp",EDGE,"E19.trimOffspring"),sQuery(id+"F2.wireOp",EDGE,"E20.trimOffspring"),sQuery(id+"F2.wireOp",EDGE,"E21.trimOffspring"),sQuery(id+"F2.wireOp",EDGE,"E22.trimOffspring"),sQuery(id+"F2.wireOp",EDGE,"E23.trimOffspring"),sQuery(id+"F2.wireOp",EDGE,"E24.trimOffspring"),sQuery(id+"F2.wireOp",EDGE,"E25.trimOffspring"),sQuery(id+"F2.wireOp",EDGE,"E26.trimOffspring"),sQuery(id+"F2.wireOp",EDGE,"E27.trimOffspring"),sQuery(id+"F2.wireOp",EDGE,"E28.trimOffspring"),sQuery(id+"F2.wireOp",EDGE,"E29")])],"isStart":false}),makeQuery(id+"F6.opExtrude","SWEPT_FACE",FACE,{"disambiguationData":[OSD([sQuery(id+"F5.wireOp",EDGE,"E34")])]})]}),makeQuery(id+"F8.opExtrude","SWEPT_FACE",FACE,{"disambiguationData":[OSD([sQuery(id+"F7.wireOp",EDGE,"E38.left")])]})]});
            var Q7;
            Q7=makeQuery(id+"F8.boolean.opBoolean","INTERSECT",EDGE,{"derivedFrom":[makeQuery(id+"F6.opExtrude","SWEPT_FACE",FACE,{"disambiguationData":[OSD([sQuery(id+"F5.wireOp",EDGE,"E30")])]}),makeQuery(id+"F8.opExtrude","SWEPT_FACE",FACE,{"disambiguationData":[OSD([sQuery(id+"F7.wireOp",EDGE,"E36.right")])]})]});
            var Q8;
            Q8=makeQuery(id+"F8.boolean.opBoolean","INTERSECT",EDGE,{"derivedFrom":[makeQuery(id+"F6.opExtrude","SWEPT_FACE",FACE,{"disambiguationData":[OSD([sQuery(id+"F5.wireOp",EDGE,"E30")])]}),makeQuery(id+"F8.opExtrude","SWEPT_FACE",FACE,{"disambiguationData":[OSD([sQuery(id+"F7.wireOp",EDGE,"E37.right")])]})]});
            fillet(context, id + "F10", {"entities" : qUnion([Q0, Q1, Q2, Q3, Q4, Q5, Q6, Q7, Q8]), "radius" : 0.25 * mm, "tangentPropagation" : true, "allowEdgeOverflow" : false});
        }
        {
            var Q0;
            Q0=makeQuery(id+"F8.boolean.opBoolean","INTERSECT",EDGE,{"derivedFrom":[makeQuery(id+"F6.opExtrude","SWEPT_FACE",FACE,{"disambiguationData":[OSD([sQuery(id+"F5.wireOp",EDGE,"E33")])]}),makeQuery(id+"F8.opExtrude","SWEPT_FACE",FACE,{"disambiguationData":[OSD([sQuery(id+"F7.wireOp",EDGE,"E37.right")])]})]});
            var Q1;
            Q1=makeQuery(id+"F8.boolean.opBoolean","INTERSECT",EDGE,{"derivedFrom":[makeQuery(id+"F6.boolean.opBoolean","MERGE",FACE,{"derivedFrom":[makeQuery(id+"F3.opExtrude","CAP_FACE",FACE,{"disambiguationData":[OSD([sQuery(id+"F2.wireOp",EDGE,"E1.bottom"),sQuery(id+"F2.wireOp",EDGE,"E1.top"),sQuery(id+"F2.wireOp",EDGE,"E1.left"),sQuery(id+"F2.wireOp",EDGE,"E1.right"),sQuery(id+"F2.wireOp",EDGE,"E2.bottom"),sQuery(id+"F2.wireOp",EDGE,"E2.top"),sQuery(id+"F2.wireOp",EDGE,"E2.left"),sQuery(id+"F2.wireOp",EDGE,"E2.right"),sQuery(id+"F2.wireOp",EDGE,"E3"),sQuery(id+"F2.wireOp",EDGE,"E4"),sQuery(id+"F2.wireOp",EDGE,"E5"),sQuery(id+"F2.wireOp",EDGE,"E6"),sQuery(id+"F2.wireOp",EDGE,"E7.trimOffspring"),sQuery(id+"F2.wireOp",EDGE,"E8.trimOffspring"),sQuery(id+"F2.wireOp",EDGE,"E9.trimOffspring"),sQuery(id+"F2.wireOp",EDGE,"E10.trimOffspring"),sQuery(id+"F2.wireOp",EDGE,"E11.trimOffspring"),sQuery(id+"F2.wireOp",EDGE,"E12.trimOffspring"),sQuery(id+"F2.wireOp",EDGE,"E13.trimOffspring"),sQuery(id+"F2.wireOp",EDGE,"E14.1.0.0"),sQuery(id+"F2.wireOp",EDGE,"E14.1.0.1"),sQuery(id+"F2.wireOp",EDGE,"E14.1.0.2"),sQuery(id+"F2.wireOp",EDGE,"E14.1.0.3"),sQuery(id+"F2.wireOp",EDGE,"E14.2.0.0"),sQuery(id+"F2.wireOp",EDGE,"E14.2.0.1"),sQuery(id+"F2.wireOp",EDGE,"E14.2.0.2"),sQuery(id+"F2.wireOp",EDGE,"E14.2.0.3"),sQuery(id+"F2.wireOp",EDGE,"E14.3.0.0"),sQuery(id+"F2.wireOp",EDGE,"E14.3.0.1"),sQuery(id+"F2.wireOp",EDGE,"E14.3.0.2"),sQuery(id+"F2.wireOp",EDGE,"E14.3.0.3"),sQuery(id+"F2.wireOp",EDGE,"E14.4.0.0"),sQuery(id+"F2.wireOp",EDGE,"E14.4.0.1"),sQuery(id+"F2.wireOp",EDGE,"E14.4.0.2"),sQuery(id+"F2.wireOp",EDGE,"E14.4.0.3"),sQuery(id+"F2.wireOp",EDGE,"E15.trimOffspring"),sQuery(id+"F2.wireOp",EDGE,"E16.trimOffspring"),sQuery(id+"F2.wireOp",EDGE,"E17.trimOffspring"),sQuery(id+"F2.wireOp",EDGE,"E18.trimOffspring"),sQuery(id+"F2.wireOp",EDGE,"E19.trimOffspring"),sQuery(id+"F2.wireOp",EDGE,"E20.trimOffspring"),sQuery(id+"F2.wireOp",EDGE,"E21.trimOffspring"),sQuery(id+"F2.wireOp",EDGE,"E22.trimOffspring"),sQuery(id+"F2.wireOp",EDGE,"E23.trimOffspring"),sQuery(id+"F2.wireOp",EDGE,"E24.trimOffspring"),sQuery(id+"F2.wireOp",EDGE,"E25.trimOffspring"),sQuery(id+"F2.wireOp",EDGE,"E26.trimOffspring"),sQuery(id+"F2.wireOp",EDGE,"E27.trimOffspring"),sQuery(id+"F2.wireOp",EDGE,"E28.trimOffspring"),sQuery(id+"F2.wireOp",EDGE,"E29")])],"isStart":false}),makeQuery(id+"F6.opExtrude","SWEPT_FACE",FACE,{"disambiguationData":[OSD([sQuery(id+"F5.wireOp",EDGE,"E34")])]})]}),makeQuery(id+"F8.opExtrude","SWEPT_FACE",FACE,{"disambiguationData":[OSD([sQuery(id+"F7.wireOp",EDGE,"E37.right")])]})]});
            var Q2;
            Q2=makeQuery(id+"F8.boolean.opBoolean","INTERSECT",EDGE,{"derivedFrom":[makeQuery(id+"F6.boolean.opBoolean","MERGE",FACE,{"derivedFrom":[makeQuery(id+"F3.opExtrude","CAP_FACE",FACE,{"disambiguationData":[OSD([sQuery(id+"F2.wireOp",EDGE,"E1.bottom"),sQuery(id+"F2.wireOp",EDGE,"E1.top"),sQuery(id+"F2.wireOp",EDGE,"E1.left"),sQuery(id+"F2.wireOp",EDGE,"E1.right"),sQuery(id+"F2.wireOp",EDGE,"E2.bottom"),sQuery(id+"F2.wireOp",EDGE,"E2.top"),sQuery(id+"F2.wireOp",EDGE,"E2.left"),sQuery(id+"F2.wireOp",EDGE,"E2.right"),sQuery(id+"F2.wireOp",EDGE,"E3"),sQuery(id+"F2.wireOp",EDGE,"E4"),sQuery(id+"F2.wireOp",EDGE,"E5"),sQuery(id+"F2.wireOp",EDGE,"E6"),sQuery(id+"F2.wireOp",EDGE,"E7.trimOffspring"),sQuery(id+"F2.wireOp",EDGE,"E8.trimOffspring"),sQuery(id+"F2.wireOp",EDGE,"E9.trimOffspring"),sQuery(id+"F2.wireOp",EDGE,"E10.trimOffspring"),sQuery(id+"F2.wireOp",EDGE,"E11.trimOffspring"),sQuery(id+"F2.wireOp",EDGE,"E12.trimOffspring"),sQuery(id+"F2.wireOp",EDGE,"E13.trimOffspring"),sQuery(id+"F2.wireOp",EDGE,"E14.1.0.0"),sQuery(id+"F2.wireOp",EDGE,"E14.1.0.1"),sQuery(id+"F2.wireOp",EDGE,"E14.1.0.2"),sQuery(id+"F2.wireOp",EDGE,"E14.1.0.3"),sQuery(id+"F2.wireOp",EDGE,"E14.2.0.0"),sQuery(id+"F2.wireOp",EDGE,"E14.2.0.1"),sQuery(id+"F2.wireOp",EDGE,"E14.2.0.2"),sQuery(id+"F2.wireOp",EDGE,"E14.2.0.3"),sQuery(id+"F2.wireOp",EDGE,"E14.3.0.0"),sQuery(id+"F2.wireOp",EDGE,"E14.3.0.1"),sQuery(id+"F2.wireOp",EDGE,"E14.3.0.2"),sQuery(id+"F2.wireOp",EDGE,"E14.3.0.3"),sQuery(id+"F2.wireOp",EDGE,"E14.4.0.0"),sQuery(id+"F2.wireOp",EDGE,"E14.4.0.1"),sQuery(id+"F2.wireOp",EDGE,"E14.4.0.2"),sQuery(id+"F2.wireOp",EDGE,"E14.4.0.3"),sQuery(id+"F2.wireOp",EDGE,"E15.trimOffspring"),sQuery(id+"F2.wireOp",EDGE,"E16.trimOffspring"),sQuery(id+"F2.wireOp",EDGE,"E17.trimOffspring"),sQuery(id+"F2.wireOp",EDGE,"E18.trimOffspring"),sQuery(id+"F2.wireOp",EDGE,"E19.trimOffspring"),sQuery(id+"F2.wireOp",EDGE,"E20.trimOffspring"),sQuery(id+"F2.wireOp",EDGE,"E21.trimOffspring"),sQuery(id+"F2.wireOp",EDGE,"E22.trimOffspring"),sQuery(id+"F2.wireOp",EDGE,"E23.trimOffspring"),sQuery(id+"F2.wireOp",EDGE,"E24.trimOffspring"),sQuery(id+"F2.wireOp",EDGE,"E25.trimOffspring"),sQuery(id+"F2.wireOp",EDGE,"E26.trimOffspring"),sQuery(id+"F2.wireOp",EDGE,"E27.trimOffspring"),sQuery(id+"F2.wireOp",EDGE,"E28.trimOffspring"),sQuery(id+"F2.wireOp",EDGE,"E29")])],"isStart":false}),makeQuery(id+"F6.opExtrude","SWEPT_FACE",FACE,{"disambiguationData":[OSD([sQuery(id+"F5.wireOp",EDGE,"E34")])]})]}),makeQuery(id+"F8.opExtrude","SWEPT_FACE",FACE,{"disambiguationData":[OSD([sQuery(id+"F7.wireOp",EDGE,"E36.right")])]})]});
            var Q3;
            Q3=makeQuery(id+"F8.boolean.opBoolean","INTERSECT",EDGE,{"derivedFrom":[makeQuery(id+"F6.opExtrude","SWEPT_FACE",FACE,{"disambiguationData":[OSD([sQuery(id+"F5.wireOp",EDGE,"E33")])]}),makeQuery(id+"F8.opExtrude","SWEPT_FACE",FACE,{"disambiguationData":[OSD([sQuery(id+"F7.wireOp",EDGE,"E36.right")])]})]});
            fillet(context, id + "F11", {"entities" : qUnion([Q0, Q1, Q2, Q3]), "radius" : 0.76 * mm, "tangentPropagation" : true, "allowEdgeOverflow" : false});
        }
        {
            var Q0;
            Q0=makeQuery(id+"F6.boolean.opBoolean","MERGE",FACE,{"derivedFrom":[makeQuery(id+"F3.opExtrude","CAP_FACE",FACE,{"disambiguationData":[OSD([sQuery(id+"F2.wireOp",EDGE,"E1.bottom"),sQuery(id+"F2.wireOp",EDGE,"E1.top"),sQuery(id+"F2.wireOp",EDGE,"E1.left"),sQuery(id+"F2.wireOp",EDGE,"E1.right"),sQuery(id+"F2.wireOp",EDGE,"E2.bottom"),sQuery(id+"F2.wireOp",EDGE,"E2.top"),sQuery(id+"F2.wireOp",EDGE,"E2.left"),sQuery(id+"F2.wireOp",EDGE,"E2.right"),sQuery(id+"F2.wireOp",EDGE,"E3"),sQuery(id+"F2.wireOp",EDGE,"E4"),sQuery(id+"F2.wireOp",EDGE,"E5"),sQuery(id+"F2.wireOp",EDGE,"E6"),sQuery(id+"F2.wireOp",EDGE,"E7.trimOffspring"),sQuery(id+"F2.wireOp",EDGE,"E8.trimOffspring"),sQuery(id+"F2.wireOp",EDGE,"E9.trimOffspring"),sQuery(id+"F2.wireOp",EDGE,"E10.trimOffspring"),sQuery(id+"F2.wireOp",EDGE,"E11.trimOffspring"),sQuery(id+"F2.wireOp",EDGE,"E12.trimOffspring"),sQuery(id+"F2.wireOp",EDGE,"E13.trimOffspring"),sQuery(id+"F2.wireOp",EDGE,"E14.1.0.0"),sQuery(id+"F2.wireOp",EDGE,"E14.1.0.1"),sQuery(id+"F2.wireOp",EDGE,"E14.1.0.2"),sQuery(id+"F2.wireOp",EDGE,"E14.1.0.3"),sQuery(id+"F2.wireOp",EDGE,"E14.2.0.0"),sQuery(id+"F2.wireOp",EDGE,"E14.2.0.1"),sQuery(id+"F2.wireOp",EDGE,"E14.2.0.2"),sQuery(id+"F2.wireOp",EDGE,"E14.2.0.3"),sQuery(id+"F2.wireOp",EDGE,"E14.3.0.0"),sQuery(id+"F2.wireOp",EDGE,"E14.3.0.1"),sQuery(id+"F2.wireOp",EDGE,"E14.3.0.2"),sQuery(id+"F2.wireOp",EDGE,"E14.3.0.3"),sQuery(id+"F2.wireOp",EDGE,"E14.4.0.0"),sQuery(id+"F2.wireOp",EDGE,"E14.4.0.1"),sQuery(id+"F2.wireOp",EDGE,"E14.4.0.2"),sQuery(id+"F2.wireOp",EDGE,"E14.4.0.3"),sQuery(id+"F2.wireOp",EDGE,"E15.trimOffspring"),sQuery(id+"F2.wireOp",EDGE,"E16.trimOffspring"),sQuery(id+"F2.wireOp",EDGE,"E17.trimOffspring"),sQuery(id+"F2.wireOp",EDGE,"E18.trimOffspring"),sQuery(id+"F2.wireOp",EDGE,"E19.trimOffspring"),sQuery(id+"F2.wireOp",EDGE,"E20.trimOffspring"),sQuery(id+"F2.wireOp",EDGE,"E21.trimOffspring"),sQuery(id+"F2.wireOp",EDGE,"E22.trimOffspring"),sQuery(id+"F2.wireOp",EDGE,"E23.trimOffspring"),sQuery(id+"F2.wireOp",EDGE,"E24.trimOffspring"),sQuery(id+"F2.wireOp",EDGE,"E25.trimOffspring"),sQuery(id+"F2.wireOp",EDGE,"E26.trimOffspring"),sQuery(id+"F2.wireOp",EDGE,"E27.trimOffspring"),sQuery(id+"F2.wireOp",EDGE,"E28.trimOffspring"),sQuery(id+"F2.wireOp",EDGE,"E29")])],"isStart":false}),makeQuery(id+"F6.opExtrude","SWEPT_FACE",FACE,{"disambiguationData":[OSD([sQuery(id+"F5.wireOp",EDGE,"E34")])]})]});
            var sketch = newSketch(context, id + "F12", { "sketchPlane" : qUnion([Q0])});
            skCircle(sketch, "E39", {"center": v(-75.18, -30.73) * mm, "radius": 3.18 * mm});
            skCircle(sketch, "E40", {"center": v(75.18, -30.73) * mm, "radius": 3.18 * mm});
            skSolve(sketch);
        }
        {
            var Q0;
            Q0 = qSketchRegion(id + "F12", true);
            var Q1;
            Q1=makeQuery(id+"F3.boolean.opBoolean","SPLIT",FACE,{"disambiguationData":[TD([makeQuery(id+"F3.opExtrude","SWEPT_FACE",FACE,{"disambiguationData":[OSD([sQuery(id+"F2.wireOp",EDGE,"E2.top")])]})])],"derivedFrom":makeQuery(id+"F1.opExtrude","CAP_FACE",FACE,{"disambiguationData":[OSD([sQuery(id+"F0.wireOp",EDGE,"E0.bottom"),sQuery(id+"F0.wireOp",EDGE,"E0.top"),sQuery(id+"F0.wireOp",EDGE,"E0.left"),sQuery(id+"F0.wireOp",EDGE,"E0.right")])],"isStart":false})});
            extrude(context, id + "F13", {"entities" : qUnion([Q0]), "operationType" : NewBodyOperationType.ADD, "endBound" : BoundingType.UP_TO_SURFACE, "oppositeDirection" : true, "endBoundEntityFace" : qUnion([Q1]), "depth" : 6.35 * mm});
        }
        {
            var Q0;
            Q0=makeQuery(id+"F13.boolean.opBoolean","MERGE",FACE,{"derivedFrom":[makeQuery(id+"F6.boolean.opBoolean","MERGE",FACE,{"derivedFrom":[makeQuery(id+"F3.opExtrude","CAP_FACE",FACE,{"disambiguationData":[OSD([sQuery(id+"F2.wireOp",EDGE,"E1.bottom"),sQuery(id+"F2.wireOp",EDGE,"E1.top"),sQuery(id+"F2.wireOp",EDGE,"E1.left"),sQuery(id+"F2.wireOp",EDGE,"E1.right"),sQuery(id+"F2.wireOp",EDGE,"E2.bottom"),sQuery(id+"F2.wireOp",EDGE,"E2.top"),sQuery(id+"F2.wireOp",EDGE,"E2.left"),sQuery(id+"F2.wireOp",EDGE,"E2.right"),sQuery(id+"F2.wireOp",EDGE,"E3"),sQuery(id+"F2.wireOp",EDGE,"E4"),sQuery(id+"F2.wireOp",EDGE,"E5"),sQuery(id+"F2.wireOp",EDGE,"E6"),sQuery(id+"F2.wireOp",EDGE,"E7.trimOffspring"),sQuery(id+"F2.wireOp",EDGE,"E8.trimOffspring"),sQuery(id+"F2.wireOp",EDGE,"E9.trimOffspring"),sQuery(id+"F2.wireOp",EDGE,"E10.trimOffspring"),sQuery(id+"F2.wireOp",EDGE,"E11.trimOffspring"),sQuery(id+"F2.wireOp",EDGE,"E12.trimOffspring"),sQuery(id+"F2.wireOp",EDGE,"E13.trimOffspring"),sQuery(id+"F2.wireOp",EDGE,"E14.1.0.0"),sQuery(id+"F2.wireOp",EDGE,"E14.1.0.1"),sQuery(id+"F2.wireOp",EDGE,"E14.1.0.2"),sQuery(id+"F2.wireOp",EDGE,"E14.1.0.3"),sQuery(id+"F2.wireOp",EDGE,"E14.2.0.0"),sQuery(id+"F2.wireOp",EDGE,"E14.2.0.1"),sQuery(id+"F2.wireOp",EDGE,"E14.2.0.2"),sQuery(id+"F2.wireOp",EDGE,"E14.2.0.3"),sQuery(id+"F2.wireOp",EDGE,"E14.3.0.0"),sQuery(id+"F2.wireOp",EDGE,"E14.3.0.1"),sQuery(id+"F2.wireOp",EDGE,"E14.3.0.2"),sQuery(id+"F2.wireOp",EDGE,"E14.3.0.3"),sQuery(id+"F2.wireOp",EDGE,"E14.4.0.0"),sQuery(id+"F2.wireOp",EDGE,"E14.4.0.1"),sQuery(id+"F2.wireOp",EDGE,"E14.4.0.2"),sQuery(id+"F2.wireOp",EDGE,"E14.4.0.3"),sQuery(id+"F2.wireOp",EDGE,"E15.trimOffspring"),sQuery(id+"F2.wireOp",EDGE,"E16.trimOffspring"),sQuery(id+"F2.wireOp",EDGE,"E17.trimOffspring"),sQuery(id+"F2.wireOp",EDGE,"E18.trimOffspring"),sQuery(id+"F2.wireOp",EDGE,"E19.trimOffspring"),sQuery(id+"F2.wireOp",EDGE,"E20.trimOffspring"),sQuery(id+"F2.wireOp",EDGE,"E21.trimOffspring"),sQuery(id+"F2.wireOp",EDGE,"E22.trimOffspring"),sQuery(id+"F2.wireOp",EDGE,"E23.trimOffspring"),sQuery(id+"F2.wireOp",EDGE,"E24.trimOffspring"),sQuery(id+"F2.wireOp",EDGE,"E25.trimOffspring"),sQuery(id+"F2.wireOp",EDGE,"E26.trimOffspring"),sQuery(id+"F2.wireOp",EDGE,"E27.trimOffspring"),sQuery(id+"F2.wireOp",EDGE,"E28.trimOffspring"),sQuery(id+"F2.wireOp",EDGE,"E29")])],"isStart":false}),makeQuery(id+"F6.opExtrude","SWEPT_FACE",FACE,{"disambiguationData":[OSD([sQuery(id+"F5.wireOp",EDGE,"E34")])]})]}),makeQuery(id+"F13.opExtrude","CAP_FACE",FACE,{"disambiguationData":[OSD([sQuery(id+"F12.wireOp",EDGE,"E39")])],"isStart":true}),makeQuery(id+"F13.opExtrude","CAP_FACE",FACE,{"disambiguationData":[OSD([sQuery(id+"F12.wireOp",EDGE,"E40")])],"isStart":true})]});
            var sketch = newSketch(context, id + "F14", { "sketchPlane" : qUnion([Q0])});
            skCircle(sketch, "E41", {"center": v(-75.18, -30.73) * mm, "radius": 2.41 * mm});
            skCircle(sketch, "E42", {"center": v(75.18, -30.73) * mm, "radius": 2.41 * mm});
            skSolve(sketch);
        }
        {
            var Q0;
            Q0 = qSketchRegion(id + "F14", true);
            extrude(context, id + "F15", {"entities" : qUnion([Q0]), "operationType" : NewBodyOperationType.REMOVE, "oppositeDirection" : true, "depth" : 3.23 * mm});
        }
        {
            var Q0;
            Q0=makeQuery(id+"F13.boolean.opBoolean","MERGE",FACE,{"derivedFrom":[makeQuery(id+"F6.boolean.opBoolean","MERGE",FACE,{"derivedFrom":[makeQuery(id+"F3.opExtrude","CAP_FACE",FACE,{"disambiguationData":[OSD([sQuery(id+"F2.wireOp",EDGE,"E1.bottom"),sQuery(id+"F2.wireOp",EDGE,"E1.top"),sQuery(id+"F2.wireOp",EDGE,"E1.left"),sQuery(id+"F2.wireOp",EDGE,"E1.right"),sQuery(id+"F2.wireOp",EDGE,"E2.bottom"),sQuery(id+"F2.wireOp",EDGE,"E2.top"),sQuery(id+"F2.wireOp",EDGE,"E2.left"),sQuery(id+"F2.wireOp",EDGE,"E2.right"),sQuery(id+"F2.wireOp",EDGE,"E3"),sQuery(id+"F2.wireOp",EDGE,"E4"),sQuery(id+"F2.wireOp",EDGE,"E5"),sQuery(id+"F2.wireOp",EDGE,"E6"),sQuery(id+"F2.wireOp",EDGE,"E7.trimOffspring"),sQuery(id+"F2.wireOp",EDGE,"E8.trimOffspring"),sQuery(id+"F2.wireOp",EDGE,"E9.trimOffspring"),sQuery(id+"F2.wireOp",EDGE,"E10.trimOffspring"),sQuery(id+"F2.wireOp",EDGE,"E11.trimOffspring"),sQuery(id+"F2.wireOp",EDGE,"E12.trimOffspring"),sQuery(id+"F2.wireOp",EDGE,"E13.trimOffspring"),sQuery(id+"F2.wireOp",EDGE,"E14.1.0.0"),sQuery(id+"F2.wireOp",EDGE,"E14.1.0.1"),sQuery(id+"F2.wireOp",EDGE,"E14.1.0.2"),sQuery(id+"F2.wireOp",EDGE,"E14.1.0.3"),sQuery(id+"F2.wireOp",EDGE,"E14.2.0.0"),sQuery(id+"F2.wireOp",EDGE,"E14.2.0.1"),sQuery(id+"F2.wireOp",EDGE,"E14.2.0.2"),sQuery(id+"F2.wireOp",EDGE,"E14.2.0.3"),sQuery(id+"F2.wireOp",EDGE,"E14.3.0.0"),sQuery(id+"F2.wireOp",EDGE,"E14.3.0.1"),sQuery(id+"F2.wireOp",EDGE,"E14.3.0.2"),sQuery(id+"F2.wireOp",EDGE,"E14.3.0.3"),sQuery(id+"F2.wireOp",EDGE,"E14.4.0.0"),sQuery(id+"F2.wireOp",EDGE,"E14.4.0.1"),sQuery(id+"F2.wireOp",EDGE,"E14.4.0.2"),sQuery(id+"F2.wireOp",EDGE,"E14.4.0.3"),sQuery(id+"F2.wireOp",EDGE,"E15.trimOffspring"),sQuery(id+"F2.wireOp",EDGE,"E16.trimOffspring"),sQuery(id+"F2.wireOp",EDGE,"E17.trimOffspring"),sQuery(id+"F2.wireOp",EDGE,"E18.trimOffspring"),sQuery(id+"F2.wireOp",EDGE,"E19.trimOffspring"),sQuery(id+"F2.wireOp",EDGE,"E20.trimOffspring"),sQuery(id+"F2.wireOp",EDGE,"E21.trimOffspring"),sQuery(id+"F2.wireOp",EDGE,"E22.trimOffspring"),sQuery(id+"F2.wireOp",EDGE,"E23.trimOffspring"),sQuery(id+"F2.wireOp",EDGE,"E24.trimOffspring"),sQuery(id+"F2.wireOp",EDGE,"E25.trimOffspring"),sQuery(id+"F2.wireOp",EDGE,"E26.trimOffspring"),sQuery(id+"F2.wireOp",EDGE,"E27.trimOffspring"),sQuery(id+"F2.wireOp",EDGE,"E28.trimOffspring"),sQuery(id+"F2.wireOp",EDGE,"E29")])],"isStart":false}),makeQuery(id+"F6.opExtrude","SWEPT_FACE",FACE,{"disambiguationData":[OSD([sQuery(id+"F5.wireOp",EDGE,"E34")])]})]}),makeQuery(id+"F13.opExtrude","CAP_FACE",FACE,{"disambiguationData":[OSD([sQuery(id+"F12.wireOp",EDGE,"E39")])],"isStart":true}),makeQuery(id+"F13.opExtrude","CAP_FACE",FACE,{"disambiguationData":[OSD([sQuery(id+"F12.wireOp",EDGE,"E40")])],"isStart":true})]});
            var sketch = newSketch(context, id + "F16", { "sketchPlane" : qUnion([Q0])});
            skLineSegment(sketch, "E43.bottom", {"start": v(-76.2, 1.02) * mm, "end": v(-51.82, 1.02) * mm});
            skLineSegment(sketch, "E43.top", {"start": v(-76.2, -1.02) * mm, "end": v(-51.82, -1.02) * mm});
            skLineSegment(sketch, "E43.left", {"start": v(-76.2, 1.02) * mm, "end": v(-76.2, -1.02) * mm});
            skLineSegment(sketch, "E43.right", {"start": v(49.78, 1.02) * mm, "end": v(49.78, -1.02) * mm});
            skLineSegment(sketch, "E44.bottom", {"start": v(-51.82, -31.75) * mm, "end": v(-49.78, -31.75) * mm});
            skLineSegment(sketch, "E44.top", {"start": v(-51.82, 31.75) * mm, "end": v(-49.78, 31.75) * mm});
            skLineSegment(sketch, "E44.left", {"start": v(-51.82, -31.75) * mm, "end": v(-51.82, -1.02) * mm});
            skLineSegment(sketch, "E44.right", {"start": v(-49.78, -31.75) * mm, "end": v(-49.78, -1.02) * mm});
            skLineSegment(sketch, "E45.bottom", {"start": v(-26.42, 31.75) * mm, "end": v(-24.38, 31.75) * mm});
            skLineSegment(sketch, "E45.top", {"start": v(-26.42, -31.75) * mm, "end": v(-24.38, -31.75) * mm});
            skLineSegment(sketch, "E45.left", {"start": v(-26.42, 31.75) * mm, "end": v(-26.42, 1.02) * mm});
            skLineSegment(sketch, "E45.right", {"start": v(-24.38, 31.75) * mm, "end": v(-24.38, 1.02) * mm});
            skLineSegment(sketch, "E46.bottom", {"start": v(-1.02, -31.75) * mm, "end": v(1.02, -31.75) * mm});
            skLineSegment(sketch, "E46.top", {"start": v(-1.02, 31.75) * mm, "end": v(1.02, 31.75) * mm});
            skLineSegment(sketch, "E46.left", {"start": v(-1.02, -31.75) * mm, "end": v(-1.02, -1.02) * mm});
            skLineSegment(sketch, "E46.right", {"start": v(1.02, -31.75) * mm, "end": v(1.02, -1.02) * mm});
            skLineSegment(sketch, "E47.bottom", {"start": v(24.38, 31.75) * mm, "end": v(26.42, 31.75) * mm});
            skLineSegment(sketch, "E47.top", {"start": v(24.38, -31.75) * mm, "end": v(26.42, -31.75) * mm});
            skLineSegment(sketch, "E47.left", {"start": v(24.38, 31.75) * mm, "end": v(24.38, 1.02) * mm});
            skLineSegment(sketch, "E47.right", {"start": v(26.42, 31.75) * mm, "end": v(26.42, 1.02) * mm});
            skLineSegment(sketch, "E48.trimOffspring", {"start": v(26.42, 1.02) * mm, "end": v(49.78, 1.02) * mm});
            skLineSegment(sketch, "E49.trimOffspring", {"start": v(24.38, -1.02) * mm, "end": v(24.38, -31.75) * mm});
            skLineSegment(sketch, "E50.trimOffspring", {"start": v(26.42, -1.02) * mm, "end": v(26.42, -31.75) * mm});
            skLineSegment(sketch, "E51.trimOffspring", {"start": v(26.42, -1.02) * mm, "end": v(49.78, -1.02) * mm});
            skLineSegment(sketch, "E52.trimOffspring", {"start": v(-1.02, 1.02) * mm, "end": v(-1.02, 31.75) * mm});
            skLineSegment(sketch, "E53.trimOffspring", {"start": v(1.02, 1.02) * mm, "end": v(24.38, 1.02) * mm});
            skLineSegment(sketch, "E54.trimOffspring", {"start": v(1.02, 1.02) * mm, "end": v(1.02, 31.75) * mm});
            skLineSegment(sketch, "E55.trimOffspring", {"start": v(1.02, -1.02) * mm, "end": v(24.38, -1.02) * mm});
            skLineSegment(sketch, "E56.trimOffspring", {"start": v(-26.42, -1.02) * mm, "end": v(-26.42, -31.75) * mm});
            skLineSegment(sketch, "E57.trimOffspring", {"start": v(-24.38, 1.02) * mm, "end": v(-1.02, 1.02) * mm});
            skLineSegment(sketch, "E58.trimOffspring", {"start": v(-24.38, -1.02) * mm, "end": v(-24.38, -31.75) * mm});
            skLineSegment(sketch, "E59.trimOffspring", {"start": v(-24.38, -1.02) * mm, "end": v(-1.02, -1.02) * mm});
            skLineSegment(sketch, "E60.trimOffspring", {"start": v(-49.78, 1.02) * mm, "end": v(-26.42, 1.02) * mm});
            skLineSegment(sketch, "E61.trimOffspring", {"start": v(-51.82, 1.02) * mm, "end": v(-51.82, 31.75) * mm});
            skLineSegment(sketch, "E62.trimOffspring", {"start": v(-49.78, 1.02) * mm, "end": v(-49.78, 31.75) * mm});
            skLineSegment(sketch, "E63.trimOffspring", {"start": v(-49.78, -1.02) * mm, "end": v(-26.42, -1.02) * mm});
            skLineSegment(sketch, "E64.bottom", {"start": v(49.78, 31.75) * mm, "end": v(51.82, 31.75) * mm});
            skLineSegment(sketch, "E64.top", {"start": v(49.78, -31.75) * mm, "end": v(51.82, -31.75) * mm});
            skLineSegment(sketch, "E64.left", {"start": v(49.78, 31.75) * mm, "end": v(49.78, 1.02) * mm});
            skLineSegment(sketch, "E64.right", {"start": v(51.82, 31.75) * mm, "end": v(51.82, -31.75) * mm});
            skLineSegment(sketch, "E65.trimOffspring", {"start": v(49.78, -1.02) * mm, "end": v(49.78, -31.75) * mm});
            skSolve(sketch);
        }
        {
            var Q0;
            Q0 = qSketchRegion(id + "F16", true);
            extrude(context, id + "F17", {"entities" : qUnion([Q0]), "operationType" : NewBodyOperationType.ADD, "depth" : 1.78 * mm});
        }
        {
            var Q0;
            Q0=makeQuery(id+"F17.opExtrude","CAP_EDGE",EDGE,{"disambiguationData":[OSD([sQuery(id+"F16.wireOp",EDGE,"E43.left")])],"isStart":false});
            var Q1;
            Q1=makeQuery(id+"F17.opExtrude","CAP_EDGE",EDGE,{"disambiguationData":[OSD([sQuery(id+"F16.wireOp",EDGE,"E44.bottom")])],"isStart":false});
            var Q2;
            Q2=makeQuery(id+"F17.opExtrude","CAP_EDGE",EDGE,{"disambiguationData":[OSD([sQuery(id+"F16.wireOp",EDGE,"E45.top")])],"isStart":false});
            var Q3;
            Q3=makeQuery(id+"F17.opExtrude","CAP_EDGE",EDGE,{"disambiguationData":[OSD([sQuery(id+"F16.wireOp",EDGE,"E46.bottom")])],"isStart":false});
            var Q4;
            Q4=makeQuery(id+"F17.opExtrude","CAP_EDGE",EDGE,{"disambiguationData":[OSD([sQuery(id+"F16.wireOp",EDGE,"E47.top")])],"isStart":false});
            var Q5;
            Q5=makeQuery(id+"F17.opExtrude","CAP_EDGE",EDGE,{"disambiguationData":[OSD([sQuery(id+"F16.wireOp",EDGE,"E47.bottom")])],"isStart":false});
            var Q6;
            Q6=makeQuery(id+"F17.opExtrude","CAP_EDGE",EDGE,{"disambiguationData":[OSD([sQuery(id+"F16.wireOp",EDGE,"E46.top")])],"isStart":false});
            var Q7;
            Q7=makeQuery(id+"F17.opExtrude","CAP_EDGE",EDGE,{"disambiguationData":[OSD([sQuery(id+"F16.wireOp",EDGE,"E45.bottom")])],"isStart":false});
            var Q8;
            Q8=makeQuery(id+"F17.opExtrude","CAP_EDGE",EDGE,{"disambiguationData":[OSD([sQuery(id+"F16.wireOp",EDGE,"E44.top")])],"isStart":false});
            var Q9;
            Q9=makeQuery(id+"F17.opExtrude","CAP_EDGE",EDGE,{"disambiguationData":[OSD([sQuery(id+"F16.wireOp",EDGE,"E64.top")])],"isStart":false});
            var Q10;
            Q10=makeQuery(id+"F17.opExtrude","CAP_EDGE",EDGE,{"disambiguationData":[OSD([sQuery(id+"F16.wireOp",EDGE,"E64.bottom")])],"isStart":false});
            chamfer(context, id + "F18", {"entities" : qUnion([Q0, Q1, Q2, Q3, Q4, Q5, Q6, Q7, Q8, Q9, Q10]), "chamferType" : ChamferType.OFFSET_ANGLE, "width" : 1.78 * mm, "oppositeDirection" : false, "angle" : 45 * degree, "tangentPropagation" : true});
        }
    });
